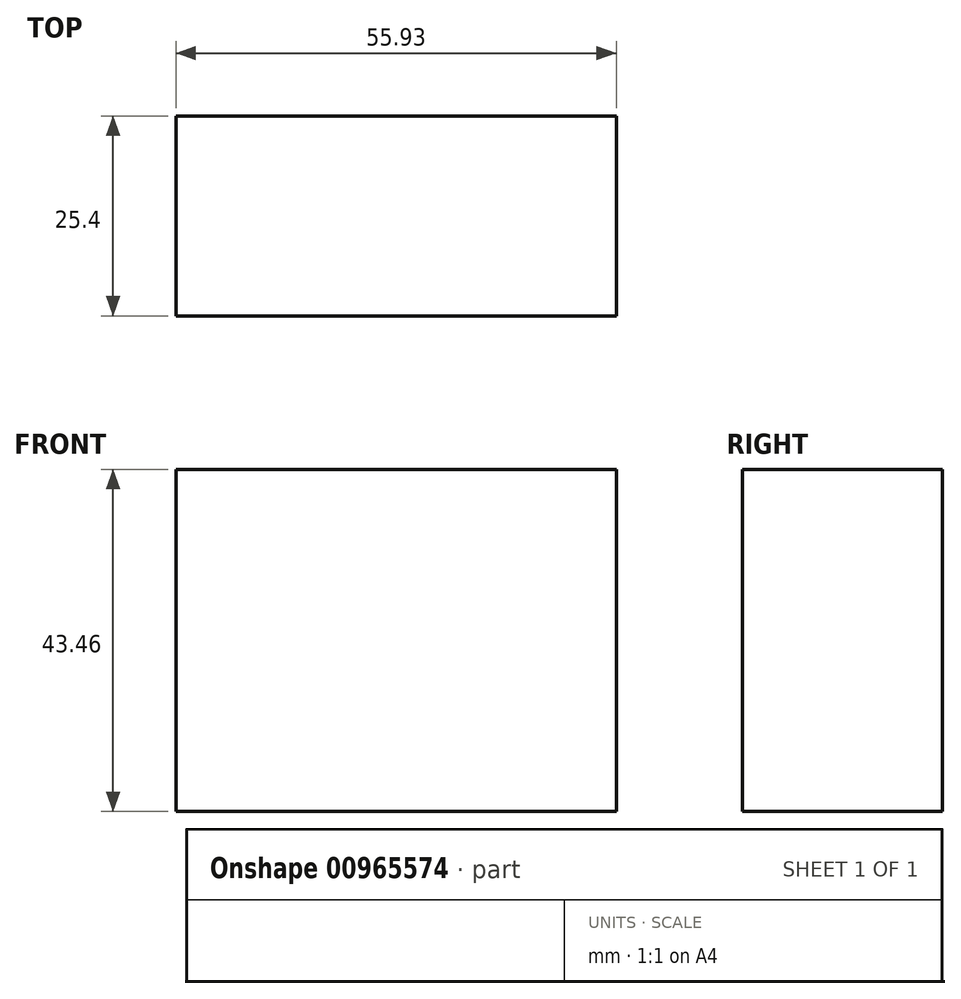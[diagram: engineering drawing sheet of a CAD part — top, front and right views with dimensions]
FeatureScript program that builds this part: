
annotation { "Feature Type Name" : "Feature", "Feature Type Description" : "" }
export const myFeature = defineFeature(function(context is Context, id is Id, definition is map)
    precondition{}
    {
        {
            var Q0;
            Q0=qCreatedBy(makeId("Front.planeOp"),FACE);
            var sketch = newSketch(context, id + "F0", { "sketchPlane" : qUnion([Q0])});
            skLineSegment(sketch, "E0.bottom", {"start": v(-24.42, 24.6) * mm, "end": v(31.51, 24.6) * mm});
            skLineSegment(sketch, "E0.top", {"start": v(-24.42, -18.87) * mm, "end": v(31.51, -18.87) * mm});
            skLineSegment(sketch, "E0.left", {"start": v(-24.42, 24.6) * mm, "end": v(-24.42, -18.87) * mm});
            skLineSegment(sketch, "E0.right", {"start": v(31.51, 24.6) * mm, "end": v(31.51, -18.87) * mm});
            skSolve(sketch);
        }
        {
            var Q0;
            Q0 = qSketchRegion(id + "F0", true);
            extrude(context, id + "F1", {"entities" : qUnion([Q0]), "oppositeDirection" : true, "depth" : 25.4 * mm, "offsetDistance" : 25.4 * mm});
        }
    });
